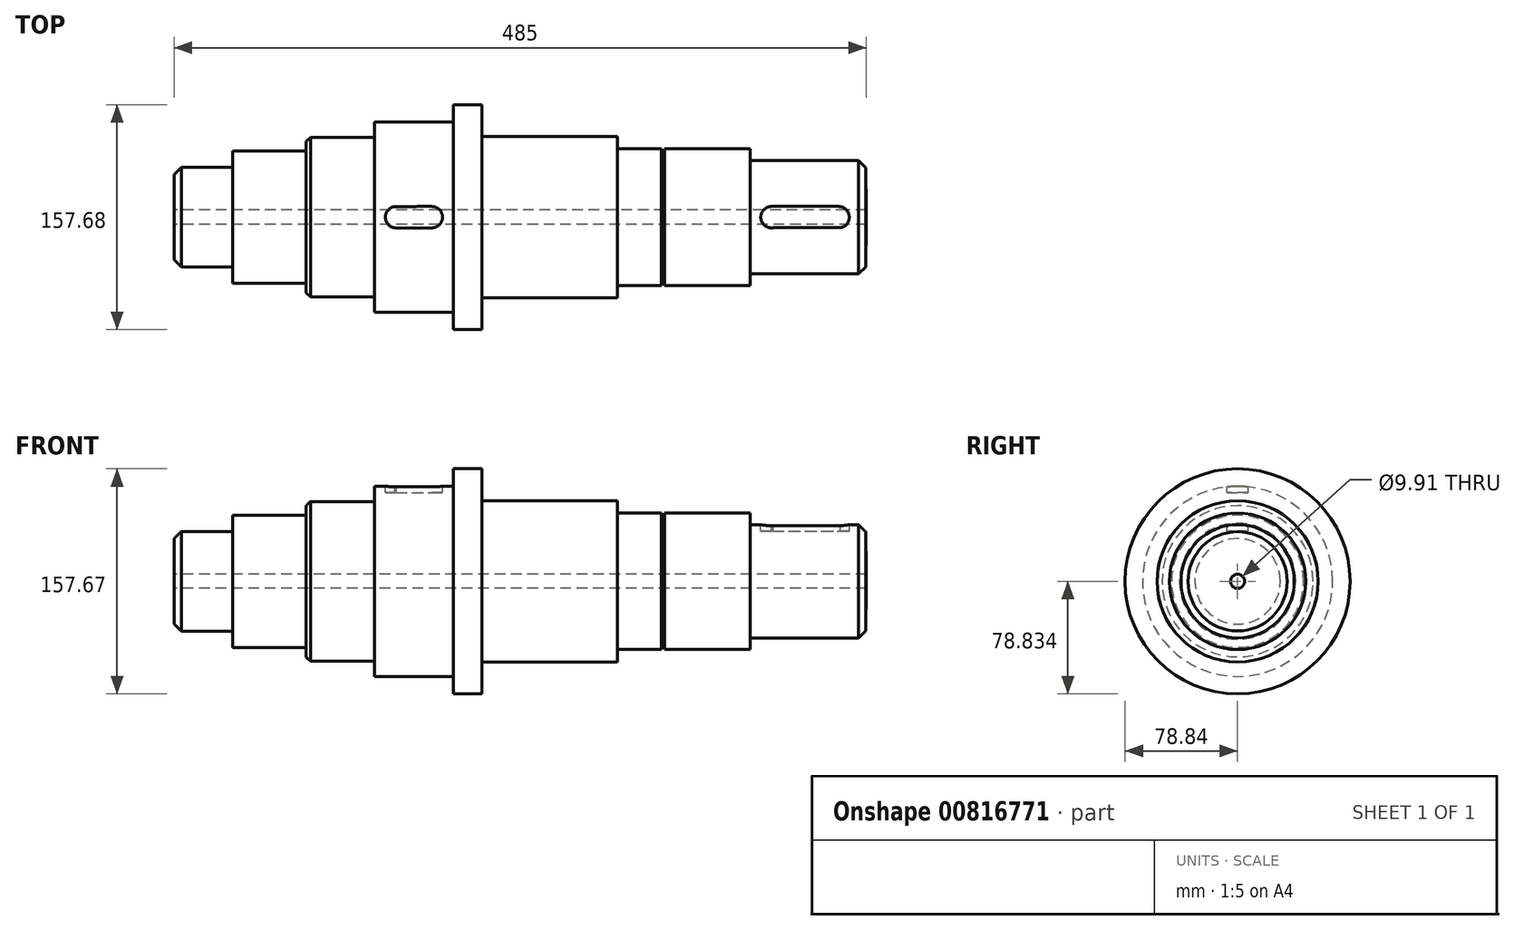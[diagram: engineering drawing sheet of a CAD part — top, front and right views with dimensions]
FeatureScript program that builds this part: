
annotation { "Feature Type Name" : "Feature", "Feature Type Description" : "" }
export const myFeature = defineFeature(function(context is Context, id is Id, definition is map)
    precondition{}
    {
        {
            var Q0;
            Q0=qCreatedBy(makeId("Front.planeOp"),FACE);
            var sketch = newSketch(context, id + "F0", { "sketchPlane" : qUnion([Q0])});
            skLineSegment(sketch, "E0", {"start": v(-232.21, -12.32) * mm, "end": v(252.79, -12.32) * mm});
            skLineSegment(sketch, "E1", {"start": v(-232.21, -12.32) * mm, "end": v(-232.21, 17.68) * mm});
            skLineSegment(sketch, "E2", {"start": v(-232.21, 17.68) * mm, "end": v(-191.21, 17.68) * mm});
            skLineSegment(sketch, "E3", {"start": v(-191.21, 17.68) * mm, "end": v(-191.21, 29) * mm});
            skLineSegment(sketch, "E4", {"start": v(-191.21, 29) * mm, "end": v(-139.71, 29) * mm});
            skLineSegment(sketch, "E5", {"start": v(-139.71, 29) * mm, "end": v(-139.71, 38.67) * mm});
            skLineSegment(sketch, "E6", {"start": v(-139.71, 38.67) * mm, "end": v(-91.71, 38.67) * mm});
            skLineSegment(sketch, "E7", {"start": v(-91.71, 38.67) * mm, "end": v(-91.71, 49.35) * mm});
            skLineSegment(sketch, "E8", {"start": v(-91.71, 49.35) * mm, "end": v(-36.71, 49.35) * mm});
            skLineSegment(sketch, "E9", {"start": v(-36.71, 49.35) * mm, "end": v(-36.71, 61.56) * mm});
            skLineSegment(sketch, "E10", {"start": v(-36.71, 61.56) * mm, "end": v(-16.71, 61.56) * mm});
            skLineSegment(sketch, "E11", {"start": v(-16.71, 61.56) * mm, "end": v(-16.71, 39.18) * mm});
            skLineSegment(sketch, "E12", {"start": v(-16.71, 39.18) * mm, "end": v(78.29, 39.18) * mm});
            skLineSegment(sketch, "E13", {"start": v(78.29, 39.18) * mm, "end": v(78.29, 30.54) * mm});
            skLineSegment(sketch, "E14", {"start": v(78.29, 30.54) * mm, "end": v(109.29, 30.54) * mm});
            skLineSegment(sketch, "E15", {"start": v(109.29, 30.54) * mm, "end": v(109.29, 23.41) * mm});
            skLineSegment(sketch, "E16", {"start": v(109.29, 23.41) * mm, "end": v(111.29, 23.41) * mm});
            skLineSegment(sketch, "E17", {"start": v(111.29, 23.41) * mm, "end": v(111.29, 30.54) * mm});
            skLineSegment(sketch, "E18", {"start": v(111.29, 30.54) * mm, "end": v(171.29, 30.54) * mm});
            skLineSegment(sketch, "E19", {"start": v(171.29, 30.54) * mm, "end": v(171.29, 22.4) * mm});
            skLineSegment(sketch, "E20", {"start": v(171.29, 22.4) * mm, "end": v(252.14, 22.4) * mm});
            skLineSegment(sketch, "E21", {"start": v(252.14, 22.4) * mm, "end": v(252.79, -12.32) * mm});
            skLineSegment(sketch, "E22", {"start": v(-232.58, -17.28) * mm, "end": v(252.65, -17.28) * mm, "construction": true});
            skSolve(sketch);
        }
        {
            var Q0;
            Q0=makeQuery(id+"F0.imprint","IMPRINT",FACE,{"disambiguationData":[TD([[makeQuery(id+"F0.imprint","IMPRINT",EDGE,{"derivedFrom":sQuery(id+"F0.wireOp",EDGE,"E0")}),1.0]])]});
            var Q1;
            Q1=sQuery(id+"F0.wireOp",EDGE,"E22");
            var Q2;
            Q2=sQuery(id+"F0.wireOp",EDGE,"E22");
            revolve(context, id + "F1", {"surfaceOperationType" : NewSurfaceOperationType.NEW, "entities" : qUnion([Q0]), "surfaceEntities" : qUnion([Q1]), "axis" : qUnion([Q2]), "revolveType" : RevolveType.FULL});
        }
        {
            var Q0;
            Q0=makeQuery(id+"F1.opRevolve","SWEPT_EDGE",EDGE,{"disambiguationData":[OSD([sQuery(id+"F0.wireOp",EDGE,"E1"),sQuery(id+"F0.wireOp",EDGE,"E2")])]});
            chamfer(context, id + "F2", {"entities" : qUnion([Q0]), "width" : 5 * mm, "tangentPropagation" : true});
        }
        {
            var Q0;
            Q0=makeQuery(id+"F1.opRevolve","SWEPT_EDGE",EDGE,{"disambiguationData":[OSD([sQuery(id+"F0.wireOp",EDGE,"E20"),sQuery(id+"F0.wireOp",EDGE,"E21")])]});
            chamfer(context, id + "F3", {"entities" : qUnion([Q0]), "width" : 5 * mm, "tangentPropagation" : true});
        }
        {
            var Q0;
            Q0=makeQuery(id+"F1.opRevolve","SWEPT_EDGE",EDGE,{"disambiguationData":[OSD([sQuery(id+"F0.wireOp",EDGE,"E5"),sQuery(id+"F0.wireOp",EDGE,"E6")])]});
            chamfer(context, id + "F4", {"entities" : qUnion([Q0]), "width" : 3 * mm, "tangentPropagation" : true});
        }
        {
            var Q0;
            Q0=qCreatedBy(makeId("Top.planeOp"),FACE);
            cPlane(context, id + "F5", {"entities" : qUnion([Q0]), "cplaneType" : CPlaneType.OFFSET, "offset" : 50 * mm, "width" : 150 * mm, "height" : 150 * mm});
        }
        {
            var Q0;
            Q0=qCreatedBy(id+"F5.planeOp",FACE);
            var sketch = newSketch(context, id + "F6", { "sketchPlane" : qUnion([Q0])});
            skArc(sketch, "E23", {"start": v(186.43, 7.5) * mm, "mid": v(178.81, -0.6) * mm, "end": v(187.64, -7.38) * mm});
            skArc(sketch, "E24", {"start": v(231.94, -7.38) * mm, "mid": v(240.76, -0.68) * mm, "end": v(233.29, 7.5) * mm});
            skLineSegment(sketch, "E25", {"start": v(186.43, 7.5) * mm, "end": v(233.29, 7.5) * mm});
            skLineSegment(sketch, "E26", {"start": v(187.64, -7.38) * mm, "end": v(234.64, -7.38) * mm});
            skSolve(sketch);
        }
        {
            var Q0;
            {var subQ1=sQuery(id+"F6.wireOp",EDGE,"E23");Q0=makeQuery(id+"F6.imprint","IMPRINT",FACE,{"disambiguationData":[TD([[makeQuery(id+"F6.imprint","IMPRINT",EDGE,{"derivedFrom":subQ1}),1.0]])]});}
            extrude(context, id + "F7", {"entities" : qUnion([Q0]), "operationType" : NewBodyOperationType.REMOVE, "oppositeDirection" : true, "depth" : 32 * mm, "offsetDistance" : 25 * mm});
        }
        {
            var Q0;
            Q0=qCreatedBy(id+"F5.planeOp",FACE);
            var sketch = newSketch(context, id + "F8", { "sketchPlane" : qUnion([Q0])});
            skArc(sketch, "E27", {"start": v(-51.71, -7.5) * mm, "mid": v(-44.21, 0) * mm, "end": v(-51.72, 7.5) * mm});
            skArc(sketch, "E28", {"start": v(-76.04, 7.47) * mm, "mid": v(-84.21, 0.2) * mm, "end": v(-76.46, -7.5) * mm});
            skLineSegment(sketch, "E29", {"start": v(-77.4, 7.47) * mm, "end": v(-51.72, 7.5) * mm});
            skLineSegment(sketch, "E30", {"start": v(-76.46, -7.5) * mm, "end": v(-51.71, -7.5) * mm});
            skSolve(sketch);
        }
        {
            var Q0;
            {var subQ1=sQuery(id+"F8.wireOp",EDGE,"E27");Q0=makeQuery(id+"F8.imprint","IMPRINT",FACE,{"disambiguationData":[TD([[makeQuery(id+"F8.imprint","IMPRINT",EDGE,{"derivedFrom":subQ1}),1.0]])]});}
            extrude(context, id + "F9", {"entities" : qUnion([Q0]), "operationType" : NewBodyOperationType.REMOVE, "oppositeDirection" : true, "depth" : 5 * mm, "offsetDistance" : 25 * mm});
        }
    });
